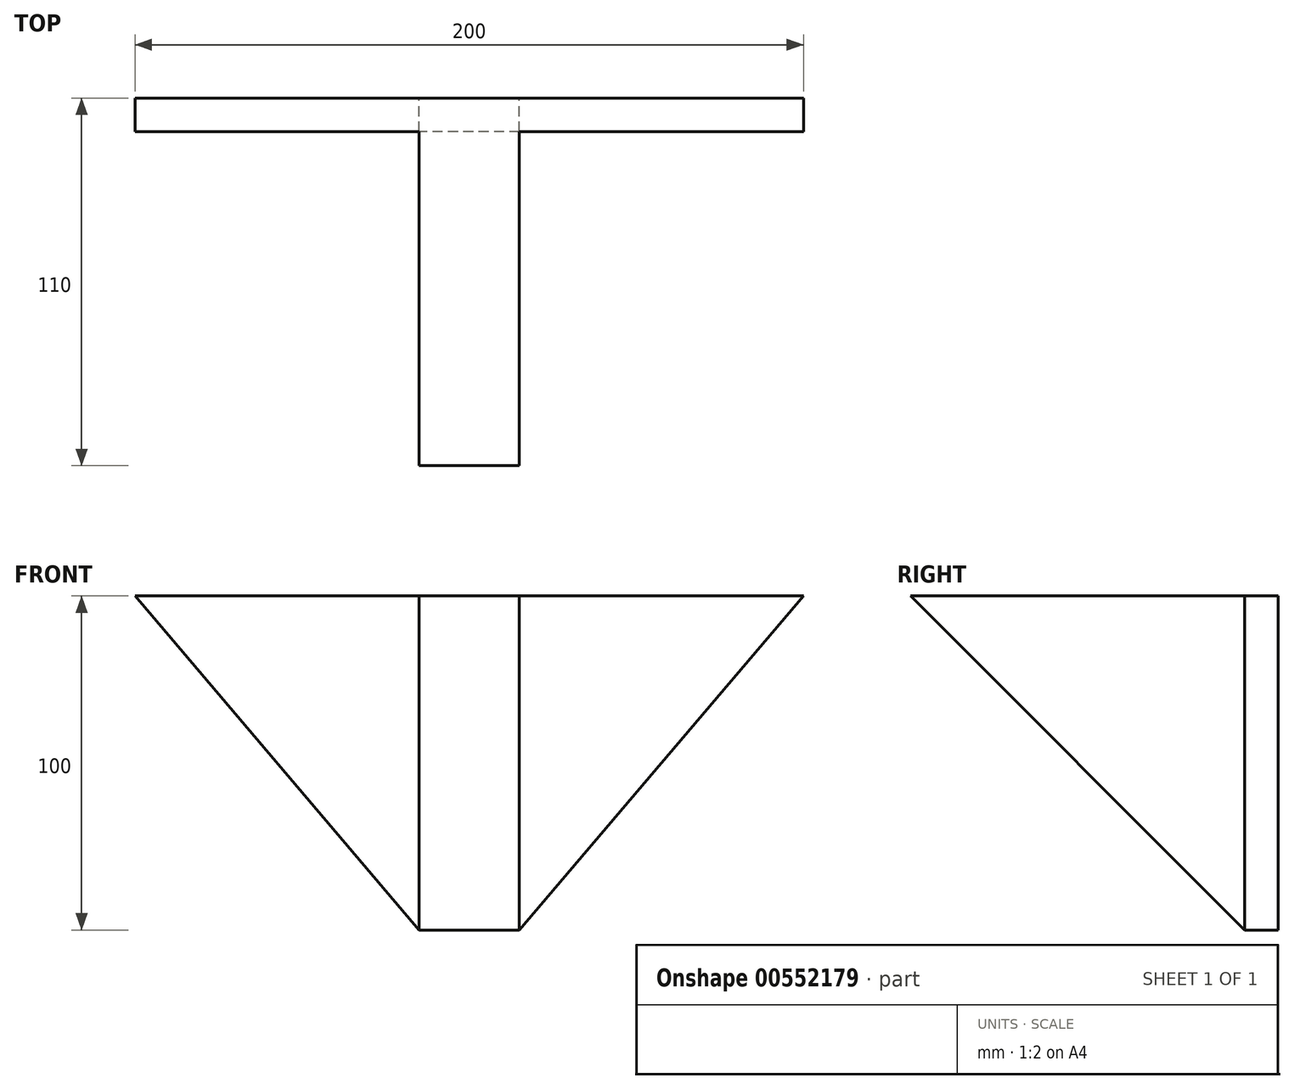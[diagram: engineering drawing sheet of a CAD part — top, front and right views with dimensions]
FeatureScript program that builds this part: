
annotation { "Feature Type Name" : "Feature", "Feature Type Description" : "" }
export const myFeature = defineFeature(function(context is Context, id is Id, definition is map)
    precondition{}
    {
        {
            var Q0;
            Q0=qCreatedBy(makeId("Front.planeOp"),FACE);
            var sketch = newSketch(context, id + "F0", { "sketchPlane" : qUnion([Q0])});
            skLineSegment(sketch, "E0", {"start": v(0, 0) * mm, "end": v(-100, 0) * mm});
            skLineSegment(sketch, "E1", {"start": v(-100, 0) * mm, "end": v(100, 0) * mm});
            skLineSegment(sketch, "E2", {"start": v(0, -100) * mm, "end": v(15, -100) * mm});
            skLineSegment(sketch, "E3", {"start": v(15, -100) * mm, "end": v(-15, -100) * mm});
            skLineSegment(sketch, "E4", {"start": v(0, 0) * mm, "end": v(0, -100) * mm});
            skLineSegment(sketch, "E5", {"start": v(-100, 0) * mm, "end": v(-15, -100) * mm});
            skLineSegment(sketch, "E6", {"start": v(15, -100) * mm, "end": v(100, 0) * mm});
            skSolve(sketch);
        }
        {
            var Q0;
            Q0 = qSketchRegion(id + "F0", true);
            extrude(context, id + "F1", {"entities" : qUnion([Q0]), "depth" : 10 * mm, "offsetDistance" : 25.4 * mm});
        }
        {
            var Q0;
            Q0=makeQuery(id+"F1.opExtrude","CAP_FACE",FACE,{"disambiguationData":[OSD([sQuery(id+"F0.wireOp",EDGE,"E1"),sQuery(id+"F0.wireOp",EDGE,"E3"),sQuery(id+"F0.wireOp",EDGE,"E5"),sQuery(id+"F0.wireOp",EDGE,"E6")])],"isStart":false});
            var sketch = newSketch(context, id + "F2", { "sketchPlane" : qUnion([Q0])});
            skLineSegment(sketch, "E7", {"start": v(-15, -100) * mm, "end": v(-15, 0) * mm});
            skLineSegment(sketch, "E8", {"start": v(15, -100) * mm, "end": v(15, 0) * mm});
            skLineSegment(sketch, "E9", {"start": v(-15, 0) * mm, "end": v(15, 0) * mm});
            skLineSegment(sketch, "E10", {"start": v(-15, -100) * mm, "end": v(15, -100) * mm});
            skSolve(sketch);
        }
        {
            var Q0;
            Q0 = qSketchRegion(id + "F2", true);
            extrude(context, id + "F3", {"entities" : qUnion([Q0]), "operationType" : NewBodyOperationType.ADD, "depth" : 100 * mm, "offsetDistance" : 25.4 * mm});
        }
        {
            var Q0;
            Q0=makeQuery(id+"F3.opExtrude","CAP_EDGE",EDGE,{"disambiguationData":[OSD([sQuery(id+"F2.wireOp",EDGE,"E10")])],"isStart":false});
            chamfer(context, id + "F4", {"entities" : qUnion([Q0]), "width" : 100 * mm, "tangentPropagation" : true});
        }
    });
